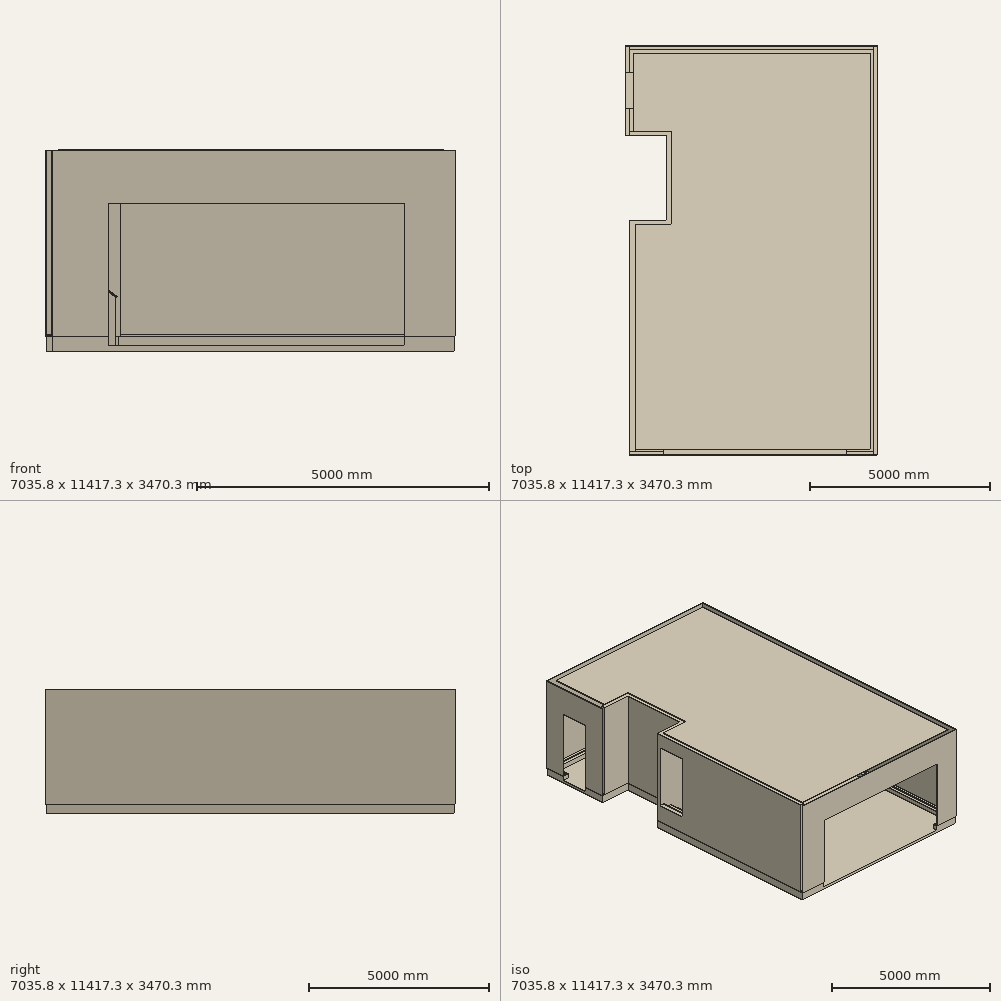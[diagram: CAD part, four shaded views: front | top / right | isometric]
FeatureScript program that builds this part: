
annotation { "Feature Type Name" : "Feature", "Feature Type Description" : "" }
export const myFeature = defineFeature(function(context is Context, id is Id, definition is map)
    precondition{}
    {
        {
            var Q0;
            Q0=qCreatedBy(makeId("Top.planeOp"),FACE);
            var sketch = newSketch(context, id + "F0", { "sketchPlane" : qUnion([Q0])});
            skLineSegment(sketch, "E0.bottom", {"start": v(0, 0) * mm, "end": v(-6597.65, 0) * mm});
            skLineSegment(sketch, "E0.top", {"start": v(0, 11023.6) * mm, "end": v(-6597.65, 11023.6) * mm});
            skLineSegment(sketch, "E0.left", {"start": v(0, 0) * mm, "end": v(0, 11023.6) * mm});
            skLineSegment(sketch, "E0.right", {"start": v(-6597.65, 0) * mm, "end": v(-6597.65, 6286.5) * mm});
            skLineSegment(sketch, "E1", {"start": v(-6597.65, 8839.2) * mm, "end": v(-5568.95, 8839.2) * mm});
            skLineSegment(sketch, "E2", {"start": v(-5568.95, 8839.2) * mm, "end": v(-5568.95, 6286.5) * mm});
            skLineSegment(sketch, "E3", {"start": v(-5568.95, 6286.5) * mm, "end": v(-6597.65, 6286.5) * mm});
            skLineSegment(sketch, "E4", {"start": v(-6597.65, 8839.2) * mm, "end": v(-6597.65, 11023.6) * mm});
            skSolve(sketch);
        }
        {
            var Q0;
            Q0 = qSketchRegion(id + "F0", true);
            extrude(context, id + "F1", {"entities" : qUnion([Q0]), "oppositeDirection" : true, "depth" : 101.6 * mm, "offsetDistance" : 25.4 * mm});
        }
        {
            var Q0;
            Q0=makeQuery(id+"F1.opExtrude","CAP_FACE",FACE,{"disambiguationData":[OSD([sQuery(id+"F0.wireOp",EDGE,"E0.bottom"),sQuery(id+"F0.wireOp",EDGE,"E0.top"),sQuery(id+"F0.wireOp",EDGE,"E0.left"),sQuery(id+"F0.wireOp",EDGE,"E0.right"),sQuery(id+"F0.wireOp",EDGE,"E1"),sQuery(id+"F0.wireOp",EDGE,"E2"),sQuery(id+"F0.wireOp",EDGE,"E3"),sQuery(id+"F0.wireOp",EDGE,"E4")])],"isStart":false});
            var sketch = newSketch(context, id + "F2", { "sketchPlane" : qUnion([Q0])});
            skLineSegment(sketch, "E5.0", {"start": v(190.5, 146.05) * mm, "end": v(-6597.65, 146.05) * mm});
            skLineSegment(sketch, "E6.0", {"start": v(0, -11023.6) * mm, "end": v(-6597.65, -11023.6) * mm});
            skLineSegment(sketch, "E7.0", {"start": v(-6807.2, -8839.2) * mm, "end": v(-6807.2, -11233.15) * mm});
            skLineSegment(sketch, "E7.1", {"start": v(190.5, -11233.15) * mm, "end": v(-6807.2, -11233.15) * mm});
            skLineSegment(sketch, "E8.0", {"start": v(190.5, 146.05) * mm, "end": v(190.5, -11233.15) * mm});
            skLineSegment(sketch, "E9", {"start": v(-6807.2, -8839.2) * mm, "end": v(-6597.65, -8839.2) * mm});
            skLineSegment(sketch, "E10", {"start": v(-6597.65, 146.05) * mm, "end": v(-6597.65, 0) * mm});
            skSolve(sketch);
        }
        {
            var Q0;
            Q0 = qSketchRegion(id + "F2", true);
            var Q1;
            Q1=makeQuery(id+"F2.imprint","IMPRINT",FACE,{"disambiguationData":[TD([[makeQuery(id+"F2.imprint","IMPRINT",EDGE,{"derivedFrom":sQuery(id+"F2.wireOp",EDGE,"E5.0")}),1.0]])]});
            extrude(context, id + "F3", {"entities" : qUnion([Q0, Q1]), "oppositeDirection" : true, "depth" : 254 * mm, "offsetDistance" : 25.4 * mm});
        }
        {
            var Q0;
            Q0=makeQuery(id+"F1.opExtrude","CAP_FACE",FACE,{"disambiguationData":[OSD([sQuery(id+"F0.wireOp",EDGE,"E0.bottom"),sQuery(id+"F0.wireOp",EDGE,"E0.top"),sQuery(id+"F0.wireOp",EDGE,"E0.left"),sQuery(id+"F0.wireOp",EDGE,"E0.right"),sQuery(id+"F0.wireOp",EDGE,"E1"),sQuery(id+"F0.wireOp",EDGE,"E2"),sQuery(id+"F0.wireOp",EDGE,"E3"),sQuery(id+"F0.wireOp",EDGE,"E4")])],"isStart":false});
            var sketch = newSketch(context, id + "F4", { "sketchPlane" : qUnion([Q0])});
            skLineSegment(sketch, "E11.0", {"start": v(-6597.65, -8839.2) * mm, "end": v(-5568.95, -8839.2) * mm});
            skLineSegment(sketch, "E12.0", {"start": v(-5568.95, -8839.2) * mm, "end": v(-5568.95, -6286.5) * mm});
            skLineSegment(sketch, "E13.0", {"start": v(-5568.95, -6286.5) * mm, "end": v(-6597.65, -6286.5) * mm});
            skLineSegment(sketch, "E14.0", {"start": v(-6597.65, 0) * mm, "end": v(-6597.65, -6286.5) * mm});
            skLineSegment(sketch, "E15.0", {"start": v(-6699.25, 146.05) * mm, "end": v(-6699.25, -6388.1) * mm});
            skLineSegment(sketch, "E15.1", {"start": v(-5670.55, -6388.1) * mm, "end": v(-6699.25, -6388.1) * mm});
            skLineSegment(sketch, "E15.2", {"start": v(-5670.55, -8737.6) * mm, "end": v(-5670.55, -6388.1) * mm});
            skLineSegment(sketch, "E15.3", {"start": v(-6807.2, -8737.6) * mm, "end": v(-5670.55, -8737.6) * mm});
            skLineSegment(sketch, "E16.0", {"start": v(-6807.2, -8839.2) * mm, "end": v(-6597.65, -8839.2) * mm});
            skLineSegment(sketch, "E17", {"start": v(-6807.2, -8839.2) * mm, "end": v(-6807.2, -8737.6) * mm});
            skLineSegment(sketch, "E18.0", {"start": v(-6597.65, 146.05) * mm, "end": v(-6597.65, 0) * mm});
            skLineSegment(sketch, "E19", {"start": v(-6597.65, 146.05) * mm, "end": v(-6699.25, 146.05) * mm});
            skSolve(sketch);
        }
        {
            var Q0;
            Q0 = qSketchRegion(id + "F4", true);
            extrude(context, id + "F5", {"entities" : qUnion([Q0]), "oppositeDirection" : true, "depth" : 254 * mm, "offsetDistance" : 25.4 * mm});
        }
        {
            var Q0;
            Q0=makeQuery(id+"F3.opExtrude","CAP_FACE",FACE,{"disambiguationData":[OSD([sQuery(id+"F0.wireOp",EDGE,"E0.bottom"),sQuery(id+"F0.wireOp",EDGE,"E0.left"),sQuery(id+"F0.wireOp",EDGE,"E4"),sQuery(id+"F2.wireOp",EDGE,"E5.0"),sQuery(id+"F2.wireOp",EDGE,"E6.0"),sQuery(id+"F2.wireOp",EDGE,"E7.0"),sQuery(id+"F2.wireOp",EDGE,"E7.1"),sQuery(id+"F2.wireOp",EDGE,"E8.0"),sQuery(id+"F2.wireOp",EDGE,"E9"),sQuery(id+"F2.wireOp",EDGE,"E10")])],"isStart":false});
            var sketch = newSketch(context, id + "F6", { "sketchPlane" : qUnion([Q0])});
            skLineSegment(sketch, "E20.bottom", {"start": v(-5746.75, 0) * mm, "end": v(-660.4, 0) * mm});
            skLineSegment(sketch, "E20.top", {"start": v(-5746.75, -146.05) * mm, "end": v(-660.4, -146.05) * mm});
            skLineSegment(sketch, "E20.left", {"start": v(-5746.75, 0) * mm, "end": v(-5746.75, -146.05) * mm});
            skLineSegment(sketch, "E20.right", {"start": v(-660.4, 0) * mm, "end": v(-660.4, -146.05) * mm});
            skSolve(sketch);
        }
        {
            var Q0;
            Q0 = qSketchRegion(id + "F6", true);
            extrude(context, id + "F7", {"entities" : qUnion([Q0]), "operationType" : NewBodyOperationType.REMOVE, "depth" : -152.4 * mm, "offsetDistance" : 25.4 * mm});
        }
        {
            var Q0;
            Q0=makeQuery(id+"F1.opExtrude","SWEPT_BODY",BODY,{"disambiguationData":[OSD([sQuery(id+"F0.wireOp",EDGE,"E0.bottom"),sQuery(id+"F0.wireOp",EDGE,"E0.top"),sQuery(id+"F0.wireOp",EDGE,"E0.left"),sQuery(id+"F0.wireOp",EDGE,"E0.right"),sQuery(id+"F0.wireOp",EDGE,"E1"),sQuery(id+"F0.wireOp",EDGE,"E2"),sQuery(id+"F0.wireOp",EDGE,"E3"),sQuery(id+"F0.wireOp",EDGE,"E4")])]});
            var Q1;
            Q1=makeQuery(id+"F3.opExtrude","SWEPT_BODY",BODY,{"disambiguationData":[OSD([sQuery(id+"F0.wireOp",EDGE,"E0.bottom"),sQuery(id+"F0.wireOp",EDGE,"E0.left"),sQuery(id+"F0.wireOp",EDGE,"E4"),sQuery(id+"F2.wireOp",EDGE,"E5.0"),sQuery(id+"F2.wireOp",EDGE,"E6.0"),sQuery(id+"F2.wireOp",EDGE,"E7.0"),sQuery(id+"F2.wireOp",EDGE,"E7.1"),sQuery(id+"F2.wireOp",EDGE,"E8.0"),sQuery(id+"F2.wireOp",EDGE,"E9"),sQuery(id+"F2.wireOp",EDGE,"E10")])]});
            var Q2;
            Q2=makeQuery(id+"F5.opExtrude","SWEPT_BODY",BODY,{"disambiguationData":[OSD([sQuery(id+"F4.wireOp",EDGE,"E11.0"),sQuery(id+"F4.wireOp",EDGE,"E12.0"),sQuery(id+"F4.wireOp",EDGE,"E13.0"),sQuery(id+"F4.wireOp",EDGE,"E14.0"),sQuery(id+"F4.wireOp",EDGE,"E15.0"),sQuery(id+"F4.wireOp",EDGE,"E15.1"),sQuery(id+"F4.wireOp",EDGE,"E15.2"),sQuery(id+"F4.wireOp",EDGE,"E15.3"),sQuery(id+"F4.wireOp",EDGE,"E16.0"),sQuery(id+"F4.wireOp",EDGE,"E17"),sQuery(id+"F4.wireOp",EDGE,"E18.0"),sQuery(id+"F4.wireOp",EDGE,"E19")])]});
            booleanBodies(context, id + "F8", {"operationType" : BooleanOperationType.UNION, "tools" : qUnion([Q0, Q1, Q2])});
        }
        {
            var Q0;
            {var subQ0=sQuery(id+"F2.wireOp",EDGE,"E5.0");var subQ2=sQuery(id+"F2.wireOp",EDGE,"E10");var subQ3=sQuery(id+"F0.wireOp",EDGE,"E0.bottom");var subQ5=sQuery(id+"F2.wireOp",EDGE,"E9");var subQ6=sQuery(id+"F2.wireOp",EDGE,"E8.0");var subQ7=sQuery(id+"F2.wireOp",EDGE,"E7.1");var subQ8=sQuery(id+"F2.wireOp",EDGE,"E7.0");var subQ9=sQuery(id+"F2.wireOp",EDGE,"E6.0");var subQ10=sQuery(id+"F0.wireOp",EDGE,"E4");var subQ11=sQuery(id+"F0.wireOp",EDGE,"E0.left");var subQ12=makeQuery(id+"F3.opExtrude","CAP_FACE",FACE,{"disambiguationData":[OSD([subQ3,subQ11,subQ10,subQ0,subQ9,subQ8,subQ7,subQ6,subQ5,subQ2])],"isStart":false});Q0=makeQuery(id+"F8.opBoolean","MERGE",FACE,{"derivedFrom":[makeQuery(id+"F5.opExtrude","CAP_FACE",FACE,{"disambiguationData":[OSD([sQuery(id+"F4.wireOp",EDGE,"E11.0"),sQuery(id+"F4.wireOp",EDGE,"E12.0"),sQuery(id+"F4.wireOp",EDGE,"E13.0"),sQuery(id+"F4.wireOp",EDGE,"E14.0"),sQuery(id+"F4.wireOp",EDGE,"E15.0"),sQuery(id+"F4.wireOp",EDGE,"E15.1"),sQuery(id+"F4.wireOp",EDGE,"E15.2"),sQuery(id+"F4.wireOp",EDGE,"E15.3"),sQuery(id+"F4.wireOp",EDGE,"E16.0"),sQuery(id+"F4.wireOp",EDGE,"E17"),sQuery(id+"F4.wireOp",EDGE,"E18.0"),sQuery(id+"F4.wireOp",EDGE,"E19")])],"isStart":false}),makeQuery(id+"F7.boolean.opBoolean","SPLIT",FACE,{"disambiguationData":[TD([makeQuery(id+"F3.opExtrude","SWEPT_FACE",FACE,{"disambiguationData":[OSD([subQ9])]})])],"derivedFrom":subQ12}),makeQuery(id+"F7.boolean.opBoolean","SPLIT",FACE,{"disambiguationData":[TD([makeQuery(id+"F3.opExtrude","SWEPT_FACE",FACE,{"disambiguationData":[OSD([subQ2])]})])],"derivedFrom":subQ12})]});}
            var sketch = newSketch(context, id + "F9", { "sketchPlane" : qUnion([Q0])});
            skLineSegment(sketch, "E21.bottom", {"start": v(-6807.2, 10490.2) * mm, "end": v(-6597.65, 10490.2) * mm});
            skLineSegment(sketch, "E21.top", {"start": v(-6807.2, 9499.6) * mm, "end": v(-6597.65, 9499.6) * mm});
            skLineSegment(sketch, "E21.left", {"start": v(-6807.2, 10490.2) * mm, "end": v(-6807.2, 9499.6) * mm});
            skLineSegment(sketch, "E21.right", {"start": v(-6597.65, 10490.2) * mm, "end": v(-6597.65, 9499.6) * mm});
            skSolve(sketch);
        }
        {
            var Q0;
            Q0=makeQuery(id+"F9.imprint","IMPRINT",FACE,{"disambiguationData":[TD([[makeQuery(id+"F9.imprint","IMPRINT",EDGE,{"derivedFrom":sQuery(id+"F9.wireOp",EDGE,"E21.bottom")}),-1.0]])]});
            extrude(context, id + "F10", {"entities" : qUnion([Q0]), "operationType" : NewBodyOperationType.REMOVE, "oppositeDirection" : true, "depth" : 152.4 * mm, "offsetDistance" : 25.4 * mm});
        }
        {
            var Q0;
            {var subQ0=sQuery(id+"F4.wireOp",EDGE,"E19");var subQ1=sQuery(id+"F0.wireOp",EDGE,"E0.left");var subQ3=sQuery(id+"F0.wireOp",EDGE,"E0.bottom");var subQ5=sQuery(id+"F2.wireOp",EDGE,"E8.0");var subQ7=sQuery(id+"F4.wireOp",EDGE,"E17");var subQ8=sQuery(id+"F0.wireOp",EDGE,"E4");var subQ10=sQuery(id+"F2.wireOp",EDGE,"E5.0");var subQ12=sQuery(id+"F2.wireOp",EDGE,"E7.1");var subQ14=sQuery(id+"F2.wireOp",EDGE,"E6.0");var subQ15=makeQuery(id+"F3.opExtrude","SWEPT_FACE",FACE,{"disambiguationData":[OSD([subQ14])]});var subQ16=sQuery(id+"F2.wireOp",EDGE,"E7.0");var subQ19=sQuery(id+"F2.wireOp",EDGE,"E10");var subQ20=sQuery(id+"F2.wireOp",EDGE,"E9");var subQ21=makeQuery(id+"F3.opExtrude","CAP_FACE",FACE,{"disambiguationData":[OSD([subQ3,subQ1,subQ8,subQ10,subQ14,subQ16,subQ12,subQ5,subQ20,subQ19])],"isStart":false});Q0=makeQuery(id+"F10.boolean.opBoolean","SPLIT",FACE,{"disambiguationData":[TD([subQ15])],"derivedFrom":makeQuery(id+"F8.opBoolean","MERGE",FACE,{"derivedFrom":[makeQuery(id+"F5.opExtrude","CAP_FACE",FACE,{"disambiguationData":[OSD([sQuery(id+"F4.wireOp",EDGE,"E11.0"),sQuery(id+"F4.wireOp",EDGE,"E12.0"),sQuery(id+"F4.wireOp",EDGE,"E13.0"),sQuery(id+"F4.wireOp",EDGE,"E14.0"),sQuery(id+"F4.wireOp",EDGE,"E15.0"),sQuery(id+"F4.wireOp",EDGE,"E15.1"),sQuery(id+"F4.wireOp",EDGE,"E15.2"),sQuery(id+"F4.wireOp",EDGE,"E15.3"),sQuery(id+"F4.wireOp",EDGE,"E16.0"),subQ7,sQuery(id+"F4.wireOp",EDGE,"E18.0"),subQ0])],"isStart":false}),makeQuery(id+"F7.boolean.opBoolean","SPLIT",FACE,{"disambiguationData":[TD([subQ15])],"derivedFrom":subQ21}),makeQuery(id+"F7.boolean.opBoolean","SPLIT",FACE,{"disambiguationData":[TD([makeQuery(id+"F3.opExtrude","SWEPT_FACE",FACE,{"disambiguationData":[OSD([subQ19])]})])],"derivedFrom":subQ21})]})});}
            var sketch = newSketch(context, id + "F11", { "sketchPlane" : qUnion([Q0])});
            skLineSegment(sketch, "E22.bottom", {"start": v(190.5, 11233.15) * mm, "end": v(101.6, 11233.15) * mm});
            skLineSegment(sketch, "E22.top", {"start": v(190.5, -146.05) * mm, "end": v(101.6, -146.05) * mm});
            skLineSegment(sketch, "E22.left", {"start": v(190.5, 11233.15) * mm, "end": v(190.5, -146.05) * mm});
            skLineSegment(sketch, "E22.right", {"start": v(101.6, 11233.15) * mm, "end": v(101.6, -146.05) * mm});
            skSolve(sketch);
        }
        {
            var Q0;
            Q0 = qSketchRegion(id + "F11", true);
            extrude(context, id + "F12", {"entities" : qUnion([Q0]), "depth" : 38.1 * mm, "offsetDistance" : 25.4 * mm});
        }
        {
            var Q0;
            {var subQ0=sQuery(id+"F4.wireOp",EDGE,"E19");var subQ1=sQuery(id+"F0.wireOp",EDGE,"E0.left");var subQ3=sQuery(id+"F0.wireOp",EDGE,"E0.bottom");var subQ5=sQuery(id+"F2.wireOp",EDGE,"E8.0");var subQ7=sQuery(id+"F4.wireOp",EDGE,"E17");var subQ8=sQuery(id+"F0.wireOp",EDGE,"E4");var subQ10=sQuery(id+"F2.wireOp",EDGE,"E5.0");var subQ12=sQuery(id+"F2.wireOp",EDGE,"E7.1");var subQ14=sQuery(id+"F2.wireOp",EDGE,"E6.0");var subQ15=makeQuery(id+"F3.opExtrude","SWEPT_FACE",FACE,{"disambiguationData":[OSD([subQ14])]});var subQ16=sQuery(id+"F2.wireOp",EDGE,"E7.0");var subQ19=sQuery(id+"F2.wireOp",EDGE,"E10");var subQ20=sQuery(id+"F2.wireOp",EDGE,"E9");var subQ21=makeQuery(id+"F3.opExtrude","CAP_FACE",FACE,{"disambiguationData":[OSD([subQ3,subQ1,subQ8,subQ10,subQ14,subQ16,subQ12,subQ5,subQ20,subQ19])],"isStart":false});Q0=makeQuery(id+"F10.boolean.opBoolean","SPLIT",FACE,{"disambiguationData":[TD([subQ15])],"derivedFrom":makeQuery(id+"F8.opBoolean","MERGE",FACE,{"derivedFrom":[makeQuery(id+"F5.opExtrude","CAP_FACE",FACE,{"disambiguationData":[OSD([sQuery(id+"F4.wireOp",EDGE,"E11.0"),sQuery(id+"F4.wireOp",EDGE,"E12.0"),sQuery(id+"F4.wireOp",EDGE,"E13.0"),sQuery(id+"F4.wireOp",EDGE,"E14.0"),sQuery(id+"F4.wireOp",EDGE,"E15.0"),sQuery(id+"F4.wireOp",EDGE,"E15.1"),sQuery(id+"F4.wireOp",EDGE,"E15.2"),sQuery(id+"F4.wireOp",EDGE,"E15.3"),sQuery(id+"F4.wireOp",EDGE,"E16.0"),subQ7,sQuery(id+"F4.wireOp",EDGE,"E18.0"),subQ0])],"isStart":false}),makeQuery(id+"F7.boolean.opBoolean","SPLIT",FACE,{"disambiguationData":[TD([subQ15])],"derivedFrom":subQ21}),makeQuery(id+"F7.boolean.opBoolean","SPLIT",FACE,{"disambiguationData":[TD([makeQuery(id+"F3.opExtrude","SWEPT_FACE",FACE,{"disambiguationData":[OSD([subQ19])]})])],"derivedFrom":subQ21})]})});}
            var sketch = newSketch(context, id + "F13", { "sketchPlane" : qUnion([Q0])});
            skLineSegment(sketch, "E23.bottom", {"start": v(-6807.2, 10490.2) * mm, "end": v(-6718.3, 10490.2) * mm});
            skLineSegment(sketch, "E23.top", {"start": v(-6807.2, 11233.15) * mm, "end": v(-6718.3, 11233.15) * mm});
            skLineSegment(sketch, "E23.left", {"start": v(-6807.2, 10490.2) * mm, "end": v(-6807.2, 11233.15) * mm});
            skLineSegment(sketch, "E23.right", {"start": v(-6718.3, 10490.2) * mm, "end": v(-6718.3, 11233.15) * mm});
            skSolve(sketch);
        }
        {
            var Q0;
            Q0 = qSketchRegion(id + "F13", true);
            extrude(context, id + "F14", {"entities" : qUnion([Q0]), "depth" : 38.1 * mm, "offsetDistance" : 25.4 * mm});
        }
        {
            var Q0;
            {var subQ0=sQuery(id+"F4.wireOp",EDGE,"E15.1");var subQ1=sQuery(id+"F0.wireOp",EDGE,"E4");var subQ3=sQuery(id+"F4.wireOp",EDGE,"E15.0");var subQ4=sQuery(id+"F4.wireOp",EDGE,"E18.0");var subQ5=sQuery(id+"F4.wireOp",EDGE,"E14.0");var subQ6=sQuery(id+"F0.wireOp",EDGE,"E0.bottom");var subQ8=sQuery(id+"F4.wireOp",EDGE,"E13.0");var subQ9=sQuery(id+"F4.wireOp",EDGE,"E16.0");var subQ10=sQuery(id+"F4.wireOp",EDGE,"E11.0");var subQ11=sQuery(id+"F4.wireOp",EDGE,"E12.0");var subQ12=sQuery(id+"F2.wireOp",EDGE,"E7.0");var subQ14=sQuery(id+"F2.wireOp",EDGE,"E5.0");var subQ16=sQuery(id+"F4.wireOp",EDGE,"E15.2");var subQ17=sQuery(id+"F4.wireOp",EDGE,"E15.3");var subQ18=sQuery(id+"F4.wireOp",EDGE,"E17");var subQ19=sQuery(id+"F4.wireOp",EDGE,"E19");var subQ21=sQuery(id+"F2.wireOp",EDGE,"E10");var subQ22=sQuery(id+"F2.wireOp",EDGE,"E9");var subQ23=sQuery(id+"F2.wireOp",EDGE,"E8.0");var subQ24=sQuery(id+"F2.wireOp",EDGE,"E7.1");var subQ25=sQuery(id+"F2.wireOp",EDGE,"E6.0");var subQ26=sQuery(id+"F0.wireOp",EDGE,"E0.left");var subQ27=makeQuery(id+"F3.opExtrude","CAP_FACE",FACE,{"disambiguationData":[OSD([subQ6,subQ26,subQ1,subQ14,subQ25,subQ12,subQ24,subQ23,subQ22,subQ21])],"isStart":false});Q0=makeQuery(id+"F10.boolean.opBoolean","SPLIT",FACE,{"disambiguationData":[TD([makeQuery(id+"F5.opExtrude","SWEPT_FACE",FACE,{"disambiguationData":[OSD([subQ11])]})])],"derivedFrom":makeQuery(id+"F8.opBoolean","MERGE",FACE,{"derivedFrom":[makeQuery(id+"F5.opExtrude","CAP_FACE",FACE,{"disambiguationData":[OSD([subQ10,subQ11,subQ8,subQ5,subQ3,subQ0,subQ16,subQ17,subQ9,subQ18,subQ4,subQ19])],"isStart":false}),makeQuery(id+"F7.boolean.opBoolean","SPLIT",FACE,{"disambiguationData":[TD([makeQuery(id+"F3.opExtrude","SWEPT_FACE",FACE,{"disambiguationData":[OSD([subQ25])]})])],"derivedFrom":subQ27}),makeQuery(id+"F7.boolean.opBoolean","SPLIT",FACE,{"disambiguationData":[TD([makeQuery(id+"F3.opExtrude","SWEPT_FACE",FACE,{"disambiguationData":[OSD([subQ21])]})])],"derivedFrom":subQ27})]})});}
            var sketch = newSketch(context, id + "F15", { "sketchPlane" : qUnion([Q0])});
            skLineSegment(sketch, "E24.bottom", {"start": v(-6807.2, 9499.6) * mm, "end": v(-6718.3, 9499.6) * mm});
            skLineSegment(sketch, "E24.top", {"start": v(-6807.2, 8737.6) * mm, "end": v(-6718.3, 8737.6) * mm});
            skLineSegment(sketch, "E24.left", {"start": v(-6807.2, 9499.6) * mm, "end": v(-6807.2, 8737.6) * mm});
            skLineSegment(sketch, "E24.right", {"start": v(-6718.3, 9499.6) * mm, "end": v(-6718.3, 8737.6) * mm});
            skSolve(sketch);
        }
        {
            var Q0;
            Q0 = qSketchRegion(id + "F15", true);
            extrude(context, id + "F16", {"entities" : qUnion([Q0]), "depth" : 25.4 * mm, "offsetDistance" : 25.4 * mm});
        }
        {
            var Q0;
            {var subQ0=sQuery(id+"F4.wireOp",EDGE,"E19");var subQ1=sQuery(id+"F0.wireOp",EDGE,"E0.left");var subQ3=sQuery(id+"F0.wireOp",EDGE,"E0.bottom");var subQ5=sQuery(id+"F2.wireOp",EDGE,"E8.0");var subQ7=sQuery(id+"F4.wireOp",EDGE,"E17");var subQ8=sQuery(id+"F0.wireOp",EDGE,"E4");var subQ10=sQuery(id+"F2.wireOp",EDGE,"E5.0");var subQ12=sQuery(id+"F2.wireOp",EDGE,"E7.1");var subQ14=sQuery(id+"F2.wireOp",EDGE,"E6.0");var subQ15=makeQuery(id+"F3.opExtrude","SWEPT_FACE",FACE,{"disambiguationData":[OSD([subQ14])]});var subQ16=sQuery(id+"F2.wireOp",EDGE,"E7.0");var subQ19=sQuery(id+"F2.wireOp",EDGE,"E10");var subQ20=sQuery(id+"F2.wireOp",EDGE,"E9");var subQ21=makeQuery(id+"F3.opExtrude","CAP_FACE",FACE,{"disambiguationData":[OSD([subQ3,subQ1,subQ8,subQ10,subQ14,subQ16,subQ12,subQ5,subQ20,subQ19])],"isStart":false});Q0=makeQuery(id+"F10.boolean.opBoolean","SPLIT",FACE,{"disambiguationData":[TD([subQ15])],"derivedFrom":makeQuery(id+"F8.opBoolean","MERGE",FACE,{"derivedFrom":[makeQuery(id+"F5.opExtrude","CAP_FACE",FACE,{"disambiguationData":[OSD([sQuery(id+"F4.wireOp",EDGE,"E11.0"),sQuery(id+"F4.wireOp",EDGE,"E12.0"),sQuery(id+"F4.wireOp",EDGE,"E13.0"),sQuery(id+"F4.wireOp",EDGE,"E14.0"),sQuery(id+"F4.wireOp",EDGE,"E15.0"),sQuery(id+"F4.wireOp",EDGE,"E15.1"),sQuery(id+"F4.wireOp",EDGE,"E15.2"),sQuery(id+"F4.wireOp",EDGE,"E15.3"),sQuery(id+"F4.wireOp",EDGE,"E16.0"),subQ7,sQuery(id+"F4.wireOp",EDGE,"E18.0"),subQ0])],"isStart":false}),makeQuery(id+"F7.boolean.opBoolean","SPLIT",FACE,{"disambiguationData":[TD([subQ15])],"derivedFrom":subQ21}),makeQuery(id+"F7.boolean.opBoolean","SPLIT",FACE,{"disambiguationData":[TD([makeQuery(id+"F3.opExtrude","SWEPT_FACE",FACE,{"disambiguationData":[OSD([subQ19])]})])],"derivedFrom":subQ21})]})});}
            var sketch = newSketch(context, id + "F17", { "sketchPlane" : qUnion([Q0])});
            skLineSegment(sketch, "E25.0", {"start": v(-6718.3, 10490.2) * mm, "end": v(-6718.3, 11233.15) * mm});
            skLineSegment(sketch, "E26.bottom", {"start": v(-6718.3, 11233.15) * mm, "end": v(101.6, 11233.15) * mm});
            skLineSegment(sketch, "E26.top", {"start": v(-6718.3, 11144.25) * mm, "end": v(101.6, 11144.25) * mm});
            skLineSegment(sketch, "E26.left", {"start": v(-6718.3, 11233.15) * mm, "end": v(-6718.3, 11144.25) * mm});
            skLineSegment(sketch, "E26.right", {"start": v(101.6, 11233.15) * mm, "end": v(101.6, 11144.25) * mm});
            skPoint(sketch, "E27.0", {"position": v(101.6, 11233.15) * mm});
            skSolve(sketch);
        }
        {
            var Q0;
            Q0 = qSketchRegion(id + "F17", true);
            extrude(context, id + "F18", {"entities" : qUnion([Q0]), "depth" : 38.1 * mm, "offsetDistance" : 25.4 * mm});
        }
        {
            var Q0;
            {var subQ0=sQuery(id+"F4.wireOp",EDGE,"E19");var subQ1=sQuery(id+"F0.wireOp",EDGE,"E0.left");var subQ3=sQuery(id+"F0.wireOp",EDGE,"E0.bottom");var subQ5=sQuery(id+"F2.wireOp",EDGE,"E8.0");var subQ7=sQuery(id+"F4.wireOp",EDGE,"E17");var subQ8=sQuery(id+"F0.wireOp",EDGE,"E4");var subQ10=sQuery(id+"F2.wireOp",EDGE,"E5.0");var subQ12=sQuery(id+"F2.wireOp",EDGE,"E7.1");var subQ14=sQuery(id+"F2.wireOp",EDGE,"E6.0");var subQ15=makeQuery(id+"F3.opExtrude","SWEPT_FACE",FACE,{"disambiguationData":[OSD([subQ14])]});var subQ16=sQuery(id+"F2.wireOp",EDGE,"E7.0");var subQ19=sQuery(id+"F2.wireOp",EDGE,"E10");var subQ20=sQuery(id+"F2.wireOp",EDGE,"E9");var subQ21=makeQuery(id+"F3.opExtrude","CAP_FACE",FACE,{"disambiguationData":[OSD([subQ3,subQ1,subQ8,subQ10,subQ14,subQ16,subQ12,subQ5,subQ20,subQ19])],"isStart":false});Q0=makeQuery(id+"F10.boolean.opBoolean","SPLIT",FACE,{"disambiguationData":[TD([subQ15])],"derivedFrom":makeQuery(id+"F8.opBoolean","MERGE",FACE,{"derivedFrom":[makeQuery(id+"F5.opExtrude","CAP_FACE",FACE,{"disambiguationData":[OSD([sQuery(id+"F4.wireOp",EDGE,"E11.0"),sQuery(id+"F4.wireOp",EDGE,"E12.0"),sQuery(id+"F4.wireOp",EDGE,"E13.0"),sQuery(id+"F4.wireOp",EDGE,"E14.0"),sQuery(id+"F4.wireOp",EDGE,"E15.0"),sQuery(id+"F4.wireOp",EDGE,"E15.1"),sQuery(id+"F4.wireOp",EDGE,"E15.2"),sQuery(id+"F4.wireOp",EDGE,"E15.3"),sQuery(id+"F4.wireOp",EDGE,"E16.0"),subQ7,sQuery(id+"F4.wireOp",EDGE,"E18.0"),subQ0])],"isStart":false}),makeQuery(id+"F7.boolean.opBoolean","SPLIT",FACE,{"disambiguationData":[TD([subQ15])],"derivedFrom":subQ21}),makeQuery(id+"F7.boolean.opBoolean","SPLIT",FACE,{"disambiguationData":[TD([makeQuery(id+"F3.opExtrude","SWEPT_FACE",FACE,{"disambiguationData":[OSD([subQ19])]})])],"derivedFrom":subQ21})]})});}
            var sketch = newSketch(context, id + "F19", { "sketchPlane" : qUnion([Q0])});
            skPoint(sketch, "E28.0", {"position": v(101.6, -146.05) * mm});
            skPoint(sketch, "E29.0", {"position": v(-660.4, -146.05) * mm});
            skLineSegment(sketch, "E30.bottom", {"start": v(-660.4, -146.05) * mm, "end": v(101.6, -146.05) * mm});
            skLineSegment(sketch, "E30.top", {"start": v(-660.4, -57.15) * mm, "end": v(101.6, -57.15) * mm});
            skLineSegment(sketch, "E30.left", {"start": v(-660.4, -146.05) * mm, "end": v(-660.4, -57.15) * mm});
            skLineSegment(sketch, "E30.right", {"start": v(101.6, -146.05) * mm, "end": v(101.6, -57.15) * mm});
            skSolve(sketch);
        }
        {
            var Q0;
            Q0 = qSketchRegion(id + "F19", true);
            extrude(context, id + "F20", {"entities" : qUnion([Q0]), "depth" : 38.1 * mm, "offsetDistance" : 25.4 * mm});
        }
        {
            var Q0;
            {var subQ0=sQuery(id+"F4.wireOp",EDGE,"E15.1");var subQ1=sQuery(id+"F0.wireOp",EDGE,"E4");var subQ3=sQuery(id+"F4.wireOp",EDGE,"E15.0");var subQ4=sQuery(id+"F4.wireOp",EDGE,"E18.0");var subQ5=sQuery(id+"F4.wireOp",EDGE,"E14.0");var subQ6=sQuery(id+"F0.wireOp",EDGE,"E0.bottom");var subQ8=sQuery(id+"F4.wireOp",EDGE,"E13.0");var subQ9=sQuery(id+"F4.wireOp",EDGE,"E16.0");var subQ10=sQuery(id+"F4.wireOp",EDGE,"E11.0");var subQ11=sQuery(id+"F4.wireOp",EDGE,"E12.0");var subQ12=sQuery(id+"F2.wireOp",EDGE,"E7.0");var subQ14=sQuery(id+"F2.wireOp",EDGE,"E5.0");var subQ16=sQuery(id+"F4.wireOp",EDGE,"E15.2");var subQ17=sQuery(id+"F4.wireOp",EDGE,"E15.3");var subQ18=sQuery(id+"F4.wireOp",EDGE,"E17");var subQ19=sQuery(id+"F4.wireOp",EDGE,"E19");var subQ21=sQuery(id+"F2.wireOp",EDGE,"E10");var subQ22=sQuery(id+"F2.wireOp",EDGE,"E9");var subQ23=sQuery(id+"F2.wireOp",EDGE,"E8.0");var subQ24=sQuery(id+"F2.wireOp",EDGE,"E7.1");var subQ25=sQuery(id+"F2.wireOp",EDGE,"E6.0");var subQ26=sQuery(id+"F0.wireOp",EDGE,"E0.left");var subQ27=makeQuery(id+"F3.opExtrude","CAP_FACE",FACE,{"disambiguationData":[OSD([subQ6,subQ26,subQ1,subQ14,subQ25,subQ12,subQ24,subQ23,subQ22,subQ21])],"isStart":false});Q0=makeQuery(id+"F10.boolean.opBoolean","SPLIT",FACE,{"disambiguationData":[TD([makeQuery(id+"F5.opExtrude","SWEPT_FACE",FACE,{"disambiguationData":[OSD([subQ11])]})])],"derivedFrom":makeQuery(id+"F8.opBoolean","MERGE",FACE,{"derivedFrom":[makeQuery(id+"F5.opExtrude","CAP_FACE",FACE,{"disambiguationData":[OSD([subQ10,subQ11,subQ8,subQ5,subQ3,subQ0,subQ16,subQ17,subQ9,subQ18,subQ4,subQ19])],"isStart":false}),makeQuery(id+"F7.boolean.opBoolean","SPLIT",FACE,{"disambiguationData":[TD([makeQuery(id+"F3.opExtrude","SWEPT_FACE",FACE,{"disambiguationData":[OSD([subQ25])]})])],"derivedFrom":subQ27}),makeQuery(id+"F7.boolean.opBoolean","SPLIT",FACE,{"disambiguationData":[TD([makeQuery(id+"F3.opExtrude","SWEPT_FACE",FACE,{"disambiguationData":[OSD([subQ21])]})])],"derivedFrom":subQ27})]})});}
            var sketch = newSketch(context, id + "F21", { "sketchPlane" : qUnion([Q0])});
            skLineSegment(sketch, "E31.bottom", {"start": v(-6699.25, -146.05) * mm, "end": v(-5746.75, -146.05) * mm});
            skLineSegment(sketch, "E31.top", {"start": v(-6699.25, -57.15) * mm, "end": v(-5746.75, -57.15) * mm});
            skLineSegment(sketch, "E31.left", {"start": v(-6699.25, -146.05) * mm, "end": v(-6699.25, -57.15) * mm});
            skLineSegment(sketch, "E31.right", {"start": v(-5746.75, -146.05) * mm, "end": v(-5746.75, -57.15) * mm});
            skSolve(sketch);
        }
        {
            var Q0;
            Q0 = qSketchRegion(id + "F21", true);
            extrude(context, id + "F22", {"entities" : qUnion([Q0]), "depth" : 38.1 * mm, "offsetDistance" : 25.4 * mm});
        }
        {
            var Q0;
            Q0=makeQuery(id+"F5.opExtrude","SWEPT_FACE",FACE,{"disambiguationData":[OSD([sQuery(id+"F4.wireOp",EDGE,"E13.0")])]});
            cPlane(context, id + "F23", {"entities" : qUnion([Q0]), "cplaneType" : CPlaneType.OFFSET, "offset" : 31.75 * mm, "width" : 152.4 * mm, "height" : 152.4 * mm});
        }
        {
            var Q0;
            Q0=qCreatedBy(id+"F23.planeOp",FACE);
            var sketch = newSketch(context, id + "F24", { "sketchPlane" : qUnion([Q0])});
            skLineSegment(sketch, "E32", {"start": v(-5746.75, 0) * mm, "end": v(-5746.75, 165.1) * mm});
            skLineSegment(sketch, "E33", {"start": v(-5746.75, 165.1) * mm, "end": v(-5708.65, 165.1) * mm});
            skLineSegment(sketch, "E34", {"start": v(-5708.65, 165.1) * mm, "end": v(-5708.65, 203.2) * mm});
            skLineSegment(sketch, "E35", {"start": v(-5708.65, 203.2) * mm, "end": v(-5994.4, 203.2) * mm});
            skLineSegment(sketch, "E36", {"start": v(-5994.4, 203.2) * mm, "end": v(-5994.4, 361.95) * mm});
            skLineSegment(sketch, "E37", {"start": v(-5994.4, 361.95) * mm, "end": v(-5962.65, 361.95) * mm});
            skLineSegment(sketch, "E38", {"start": v(-5962.65, 361.95) * mm, "end": v(-5962.65, 400.05) * mm});
            skLineSegment(sketch, "E39", {"start": v(-5962.65, 400.05) * mm, "end": v(-6248.4, 400.05) * mm});
            skLineSegment(sketch, "E40", {"start": v(-6248.4, 400.05) * mm, "end": v(-6248.4, 565.15) * mm});
            skLineSegment(sketch, "E41", {"start": v(-6248.4, 565.15) * mm, "end": v(-6235.7, 565.15) * mm});
            skLineSegment(sketch, "E42", {"start": v(-6235.7, 565.15) * mm, "end": v(-6235.7, 603.25) * mm});
            skLineSegment(sketch, "E43", {"start": v(-6235.7, 603.25) * mm, "end": v(-6521.45, 603.25) * mm});
            skLineSegment(sketch, "E44", {"start": v(-6546.85, 0) * mm, "end": v(-5746.75, 0) * mm});
            skLineSegment(sketch, "E45", {"start": v(-6521.45, 603.25) * mm, "end": v(-6521.45, 755.65) * mm});
            skLineSegment(sketch, "E46", {"start": v(-6521.45, 755.65) * mm, "end": v(-6546.85, 755.65) * mm});
            skLineSegment(sketch, "E47", {"start": v(-6546.85, 755.65) * mm, "end": v(-6546.85, 0) * mm});
            skLineSegment(sketch, "E48.0", {"start": v(-6597.65, 152.4) * mm, "end": v(-6597.65, 0) * mm});
            skSolve(sketch);
        }
        {
            var Q0;
            {var subQ0=sQuery(id+"F24.wireOp",EDGE,"E44");Q0=makeQuery(id+"F24.imprint","IMPRINT",FACE,{"disambiguationData":[TD([[makeQuery(id+"F24.imprint","IMPRINT",EDGE,{"derivedFrom":subQ0}),-1.0]])]});}
            var Q1;
            {var subQ0=sQuery(id+"F24.wireOp",EDGE,"E33");Q1=makeQuery(id+"F24.imprint","IMPRINT",FACE,{"disambiguationData":[TD([[makeQuery(id+"F24.imprint","IMPRINT",EDGE,{"derivedFrom":subQ0}),1.0]])]});}
            extrude(context, id + "F25", {"entities" : qUnion([Q0, Q1]), "depth" : 1003.3 * mm, "offsetDistance" : 25.4 * mm});
        }
        {
            var Q0;
            Q0=makeQuery(id+"F25.opExtrude","CAP_FACE",FACE,{"disambiguationData":[OSD([sQuery(id+"F24.wireOp",EDGE,"E32"),sQuery(id+"F24.wireOp",EDGE,"E33"),sQuery(id+"F24.wireOp",EDGE,"E34"),sQuery(id+"F24.wireOp",EDGE,"E35"),sQuery(id+"F24.wireOp",EDGE,"E36"),sQuery(id+"F24.wireOp",EDGE,"E37"),sQuery(id+"F24.wireOp",EDGE,"E38"),sQuery(id+"F24.wireOp",EDGE,"E39"),sQuery(id+"F24.wireOp",EDGE,"E40"),sQuery(id+"F24.wireOp",EDGE,"E41"),sQuery(id+"F24.wireOp",EDGE,"E42"),sQuery(id+"F24.wireOp",EDGE,"E43"),sQuery(id+"F24.wireOp",EDGE,"E44"),sQuery(id+"F24.wireOp",EDGE,"E45"),sQuery(id+"F24.wireOp",EDGE,"E46"),sQuery(id+"F24.wireOp",EDGE,"E47"),sQuery(id+"F24.wireOp",EDGE,"E48.0")])],"isStart":false});
            var sketch = newSketch(context, id + "F26", { "sketchPlane" : qUnion([Q0])});
            skLineSegment(sketch, "E49", {"start": v(-6546.85, 0) * mm, "end": v(-5632.45, 0) * mm});
            skLineSegment(sketch, "E50", {"start": v(-5632.45, 0) * mm, "end": v(-5632.45, 844.55) * mm});
            skLineSegment(sketch, "E51", {"start": v(-5632.45, 844.55) * mm, "end": v(-6546.85, 1479.55) * mm});
            skLineSegment(sketch, "E52", {"start": v(-6546.85, 1479.55) * mm, "end": v(-6546.85, 0) * mm});
            skSolve(sketch);
        }
        {
            var Q0;
            {var subQ2=sQuery(id+"F26.wireOp",EDGE,"E50");Q0=makeQuery(id+"F26.imprint","IMPRINT",FACE,{"disambiguationData":[TD([[makeQuery(id+"F26.imprint","IMPRINT",EDGE,{"derivedFrom":subQ2}),1.0]])]});}
            var Q1;
            {var subQ3=makeQuery(id+"F25.opExtrude","CAP_EDGE",EDGE,{"disambiguationData":[OSD([sQuery(id+"F24.wireOp",EDGE,"E32")])],"isStart":false});Q1=makeQuery(id+"F26.imprint","IMPRINT",FACE,{"disambiguationData":[TD([[makeQuery(id+"F26.imprint","IMPRINT",EDGE,{"derivedFrom":subQ3}),1.0]])]});}
            extrude(context, id + "F27", {"entities" : qUnion([Q0, Q1]), "depth" : 127 * mm, "offsetDistance" : 25.4 * mm});
        }
        {
            var Q0;
            Q0=makeQuery(id+"F27.opExtrude","CAP_FACE",FACE,{"disambiguationData":[OSD([sQuery(id+"F26.wireOp",EDGE,"E49"),sQuery(id+"F26.wireOp",EDGE,"E50"),sQuery(id+"F26.wireOp",EDGE,"E51"),sQuery(id+"F26.wireOp",EDGE,"E52")])],"isStart":false});
            var sketch = newSketch(context, id + "F28", { "sketchPlane" : qUnion([Q0])});
            skLineSegment(sketch, "E53", {"start": v(-6546.85, 1479.55) * mm, "end": v(-6546.85, 1502.74) * mm});
            skLineSegment(sketch, "E54", {"start": v(-6546.85, 1502.74) * mm, "end": v(-5595.94, 842.39) * mm});
            skLineSegment(sketch, "E55.0", {"start": v(-5632.45, 844.55) * mm, "end": v(-6546.85, 1479.55) * mm});
            skLineSegment(sketch, "E56", {"start": v(-5632.45, 844.55) * mm, "end": v(-5595.94, 819.2) * mm});
            skLineSegment(sketch, "E57", {"start": v(-5595.94, 819.2) * mm, "end": v(-5595.94, 842.39) * mm});
            skSolve(sketch);
        }
        {
            var Q0;
            Q0 = qSketchRegion(id + "F28", true);
            extrude(context, id + "F29", {"entities" : qUnion([Q0]), "operationType" : NewBodyOperationType.ADD, "depth" : 25.4 * mm, "offsetDistance" : 25.4 * mm, "hasSecondDirection" : true, "secondDirectionOppositeDirection" : true, "secondDirectionDepth" : 158.75 * mm});
        }
        {
            var Q0;
            {var subQ0=sQuery(id+"F4.wireOp",EDGE,"E15.1");var subQ1=sQuery(id+"F0.wireOp",EDGE,"E4");var subQ3=sQuery(id+"F4.wireOp",EDGE,"E15.0");var subQ4=sQuery(id+"F4.wireOp",EDGE,"E18.0");var subQ5=sQuery(id+"F4.wireOp",EDGE,"E14.0");var subQ6=sQuery(id+"F0.wireOp",EDGE,"E0.bottom");var subQ8=sQuery(id+"F4.wireOp",EDGE,"E13.0");var subQ9=sQuery(id+"F4.wireOp",EDGE,"E16.0");var subQ10=sQuery(id+"F4.wireOp",EDGE,"E11.0");var subQ11=sQuery(id+"F4.wireOp",EDGE,"E12.0");var subQ12=sQuery(id+"F2.wireOp",EDGE,"E7.0");var subQ14=sQuery(id+"F2.wireOp",EDGE,"E5.0");var subQ16=sQuery(id+"F4.wireOp",EDGE,"E15.2");var subQ17=sQuery(id+"F4.wireOp",EDGE,"E15.3");var subQ18=sQuery(id+"F4.wireOp",EDGE,"E17");var subQ19=sQuery(id+"F4.wireOp",EDGE,"E19");var subQ21=sQuery(id+"F2.wireOp",EDGE,"E10");var subQ22=sQuery(id+"F2.wireOp",EDGE,"E9");var subQ23=sQuery(id+"F2.wireOp",EDGE,"E8.0");var subQ24=sQuery(id+"F2.wireOp",EDGE,"E7.1");var subQ25=sQuery(id+"F2.wireOp",EDGE,"E6.0");var subQ26=sQuery(id+"F0.wireOp",EDGE,"E0.left");var subQ27=makeQuery(id+"F3.opExtrude","CAP_FACE",FACE,{"disambiguationData":[OSD([subQ6,subQ26,subQ1,subQ14,subQ25,subQ12,subQ24,subQ23,subQ22,subQ21])],"isStart":false});Q0=makeQuery(id+"F10.boolean.opBoolean","SPLIT",FACE,{"disambiguationData":[TD([makeQuery(id+"F5.opExtrude","SWEPT_FACE",FACE,{"disambiguationData":[OSD([subQ11])]})])],"derivedFrom":makeQuery(id+"F8.opBoolean","MERGE",FACE,{"derivedFrom":[makeQuery(id+"F5.opExtrude","CAP_FACE",FACE,{"disambiguationData":[OSD([subQ10,subQ11,subQ8,subQ5,subQ3,subQ0,subQ16,subQ17,subQ9,subQ18,subQ4,subQ19])],"isStart":false}),makeQuery(id+"F7.boolean.opBoolean","SPLIT",FACE,{"disambiguationData":[TD([makeQuery(id+"F3.opExtrude","SWEPT_FACE",FACE,{"disambiguationData":[OSD([subQ25])]})])],"derivedFrom":subQ27}),makeQuery(id+"F7.boolean.opBoolean","SPLIT",FACE,{"disambiguationData":[TD([makeQuery(id+"F3.opExtrude","SWEPT_FACE",FACE,{"disambiguationData":[OSD([subQ21])]})])],"derivedFrom":subQ27})]})});}
            var sketch = newSketch(context, id + "F30", { "sketchPlane" : qUnion([Q0])});
            skLineSegment(sketch, "E58", {"start": v(-6718.3, 8870.95) * mm, "end": v(-5537.2, 8870.95) * mm});
            skLineSegment(sketch, "E59", {"start": v(-5537.2, 8870.95) * mm, "end": v(-5537.2, 6254.75) * mm});
            skLineSegment(sketch, "E60", {"start": v(-5537.2, 6254.75) * mm, "end": v(-6546.85, 6254.75) * mm});
            skLineSegment(sketch, "E61", {"start": v(-6546.85, 6254.75) * mm, "end": v(-6546.85, -57.15) * mm});
            skLineSegment(sketch, "E62.0", {"start": v(-6699.25, -57.15) * mm, "end": v(-5746.75, -57.15) * mm});
            skLineSegment(sketch, "E63.0", {"start": v(-6699.25, -57.15) * mm, "end": v(-6699.25, 6388.1) * mm});
            skLineSegment(sketch, "E64.0", {"start": v(-5670.55, 6388.1) * mm, "end": v(-6699.25, 6388.1) * mm});
            skLineSegment(sketch, "E65.0", {"start": v(-5670.55, 8737.6) * mm, "end": v(-5670.55, 6388.1) * mm});
            skLineSegment(sketch, "E66.0", {"start": v(-6718.3, 8737.6) * mm, "end": v(-5670.55, 8737.6) * mm});
            skLineSegment(sketch, "E67.0", {"start": v(-6718.3, 8870.95) * mm, "end": v(-6718.3, 8737.6) * mm});
            skSolve(sketch);
        }
        {
            var Q0;
            Q0 = qSketchRegion(id + "F30", true);
            extrude(context, id + "F31", {"entities" : qUnion([Q0]), "depth" : 3200.4 * mm, "offsetDistance" : 25.4 * mm});
        }
        {
            var Q0;
            {var subQ0=sQuery(id+"F4.wireOp",EDGE,"E19");var subQ1=sQuery(id+"F0.wireOp",EDGE,"E0.left");var subQ3=sQuery(id+"F0.wireOp",EDGE,"E0.bottom");var subQ5=sQuery(id+"F2.wireOp",EDGE,"E8.0");var subQ7=sQuery(id+"F4.wireOp",EDGE,"E17");var subQ8=sQuery(id+"F0.wireOp",EDGE,"E4");var subQ10=sQuery(id+"F2.wireOp",EDGE,"E5.0");var subQ12=sQuery(id+"F2.wireOp",EDGE,"E7.1");var subQ14=sQuery(id+"F2.wireOp",EDGE,"E6.0");var subQ15=makeQuery(id+"F3.opExtrude","SWEPT_FACE",FACE,{"disambiguationData":[OSD([subQ14])]});var subQ16=sQuery(id+"F2.wireOp",EDGE,"E7.0");var subQ19=sQuery(id+"F2.wireOp",EDGE,"E10");var subQ20=sQuery(id+"F2.wireOp",EDGE,"E9");var subQ21=makeQuery(id+"F3.opExtrude","CAP_FACE",FACE,{"disambiguationData":[OSD([subQ3,subQ1,subQ8,subQ10,subQ14,subQ16,subQ12,subQ5,subQ20,subQ19])],"isStart":false});Q0=makeQuery(id+"F10.boolean.opBoolean","SPLIT",FACE,{"disambiguationData":[TD([subQ15])],"derivedFrom":makeQuery(id+"F8.opBoolean","MERGE",FACE,{"derivedFrom":[makeQuery(id+"F5.opExtrude","CAP_FACE",FACE,{"disambiguationData":[OSD([sQuery(id+"F4.wireOp",EDGE,"E11.0"),sQuery(id+"F4.wireOp",EDGE,"E12.0"),sQuery(id+"F4.wireOp",EDGE,"E13.0"),sQuery(id+"F4.wireOp",EDGE,"E14.0"),sQuery(id+"F4.wireOp",EDGE,"E15.0"),sQuery(id+"F4.wireOp",EDGE,"E15.1"),sQuery(id+"F4.wireOp",EDGE,"E15.2"),sQuery(id+"F4.wireOp",EDGE,"E15.3"),sQuery(id+"F4.wireOp",EDGE,"E16.0"),subQ7,sQuery(id+"F4.wireOp",EDGE,"E18.0"),subQ0])],"isStart":false}),makeQuery(id+"F7.boolean.opBoolean","SPLIT",FACE,{"disambiguationData":[TD([subQ15])],"derivedFrom":subQ21}),makeQuery(id+"F7.boolean.opBoolean","SPLIT",FACE,{"disambiguationData":[TD([makeQuery(id+"F3.opExtrude","SWEPT_FACE",FACE,{"disambiguationData":[OSD([subQ19])]})])],"derivedFrom":subQ21})]})});}
            var sketch = newSketch(context, id + "F32", { "sketchPlane" : qUnion([Q0])});
            skLineSegment(sketch, "E68.0", {"start": v(-6807.2, 8737.6) * mm, "end": v(-6807.2, 11233.15) * mm});
            skLineSegment(sketch, "E69.0", {"start": v(190.5, -146.05) * mm, "end": v(190.5, 11233.15) * mm});
            skLineSegment(sketch, "E70", {"start": v(190.5, 11233.15) * mm, "end": v(-6807.2, 11233.15) * mm});
            skPoint(sketch, "E71.0", {"position": v(-660.4, -146.05) * mm});
            skLineSegment(sketch, "E72", {"start": v(190.5, -146.05) * mm, "end": v(-660.4, -146.05) * mm});
            skLineSegment(sketch, "E73.0", {"start": v(209.55, -165.1) * mm, "end": v(-6699.25, -165.1) * mm});
            skLineSegment(sketch, "E73.1", {"start": v(209.55, -165.1) * mm, "end": v(209.55, 11252.2) * mm});
            skLineSegment(sketch, "E73.2", {"start": v(209.55, 11252.2) * mm, "end": v(-6826.25, 11252.2) * mm});
            skLineSegment(sketch, "E73.3", {"start": v(-6826.25, 8737.6) * mm, "end": v(-6826.25, 11252.2) * mm});
            skLineSegment(sketch, "E74", {"start": v(-6807.2, 8737.6) * mm, "end": v(-6826.25, 8737.6) * mm});
            skLineSegment(sketch, "E75", {"start": v(-660.4, -146.05) * mm, "end": v(-6699.25, -146.05) * mm});
            skPoint(sketch, "E76.0", {"position": v(-6699.25, -146.05) * mm});
            skLineSegment(sketch, "E77", {"start": v(-6699.25, -146.05) * mm, "end": v(-6699.25, -165.1) * mm});
            skSolve(sketch);
        }
        {
            var Q0;
            Q0 = qSketchRegion(id + "F32", true);
            extrude(context, id + "F33", {"entities" : qUnion([Q0]), "depth" : 3200.4 * mm, "offsetDistance" : 25.4 * mm});
        }
        {
            var Q0;
            Q0=makeQuery(id+"F33.opExtrude","SWEPT_FACE",FACE,{"disambiguationData":[OSD([sQuery(id+"F32.wireOp",EDGE,"E73.0")])]});
            var sketch = newSketch(context, id + "F34", { "sketchPlane" : qUnion([Q0])});
            skPoint(sketch, "E78.0", {"position": v(-5746.75, 152.4) * mm});
            skPoint(sketch, "E79.0", {"position": v(-660.4, 152.4) * mm});
            skLineSegment(sketch, "E80.bottom", {"start": v(-5746.75, 152.4) * mm, "end": v(-660.4, 152.4) * mm});
            skLineSegment(sketch, "E80.top", {"start": v(-5746.75, 2438.4) * mm, "end": v(-660.4, 2438.4) * mm});
            skLineSegment(sketch, "E80.left", {"start": v(-5746.75, 152.4) * mm, "end": v(-5746.75, 2438.4) * mm});
            skLineSegment(sketch, "E80.right", {"start": v(-660.4, 152.4) * mm, "end": v(-660.4, 2438.4) * mm});
            skSolve(sketch);
        }
        {
            var Q0;
            Q0 = qSketchRegion(id + "F34", true);
            extrude(context, id + "F35", {"entities" : qUnion([Q0]), "operationType" : NewBodyOperationType.REMOVE, "endBound" : BoundingType.UP_TO_NEXT, "oppositeDirection" : true, "depth" : 25.4 * mm, "offsetDistance" : 25.4 * mm});
        }
        {
            var Q0;
            Q0=makeQuery(id+"F33.opExtrude","SWEPT_FACE",FACE,{"disambiguationData":[OSD([sQuery(id+"F32.wireOp",EDGE,"E73.3")])]});
            var sketch = newSketch(context, id + "F36", { "sketchPlane" : qUnion([Q0])});
            skPoint(sketch, "E81.0", {"position": v(-10490.2, 152.4) * mm});
            skPoint(sketch, "E82.0", {"position": v(-9499.6, 152.4) * mm});
            skLineSegment(sketch, "E83.bottom", {"start": v(-10490.2, 152.4) * mm, "end": v(-9499.6, 152.4) * mm});
            skLineSegment(sketch, "E83.top", {"start": v(-10490.2, 2438.4) * mm, "end": v(-9499.6, 2438.4) * mm});
            skLineSegment(sketch, "E83.left", {"start": v(-10490.2, 152.4) * mm, "end": v(-10490.2, 2438.4) * mm});
            skLineSegment(sketch, "E83.right", {"start": v(-9499.6, 152.4) * mm, "end": v(-9499.6, 2438.4) * mm});
            skSolve(sketch);
        }
        {
            var Q0;
            Q0 = qSketchRegion(id + "F36", true);
            extrude(context, id + "F37", {"entities" : qUnion([Q0]), "operationType" : NewBodyOperationType.REMOVE, "endBound" : BoundingType.UP_TO_NEXT, "oppositeDirection" : true, "depth" : 25.4 * mm, "offsetDistance" : 25.4 * mm});
        }
        {
            var Q0;
            Q0=makeQuery(id+"F31.opExtrude","SWEPT_FACE",FACE,{"disambiguationData":[OSD([sQuery(id+"F30.wireOp",EDGE,"E61")])]});
            var sketch = newSketch(context, id + "F38", { "sketchPlane" : qUnion([Q0])});
            skPoint(sketch, "E84.0", {"position": v(6254.75, 755.65) * mm});
            skPoint(sketch, "E85.0", {"position": v(5251.45, 755.65) * mm});
            skLineSegment(sketch, "E86.bottom", {"start": v(6254.75, 755.65) * mm, "end": v(5251.45, 755.65) * mm});
            skLineSegment(sketch, "E86.top", {"start": v(6254.75, 2889.25) * mm, "end": v(5251.45, 2889.25) * mm});
            skLineSegment(sketch, "E86.left", {"start": v(6254.75, 755.65) * mm, "end": v(6254.75, 2889.25) * mm});
            skLineSegment(sketch, "E86.right", {"start": v(5251.45, 755.65) * mm, "end": v(5251.45, 2889.25) * mm});
            skSolve(sketch);
        }
        {
            var Q0;
            Q0 = qSketchRegion(id + "F38", true);
            extrude(context, id + "F39", {"entities" : qUnion([Q0]), "operationType" : NewBodyOperationType.REMOVE, "endBound" : BoundingType.UP_TO_NEXT, "oppositeDirection" : true, "depth" : 25.4 * mm, "offsetDistance" : 25.4 * mm});
        }
        {
            var Q0;
            Q0=makeQuery(id+"F31.opExtrude","CAP_FACE",FACE,{"disambiguationData":[OSD([sQuery(id+"F30.wireOp",EDGE,"E58"),sQuery(id+"F30.wireOp",EDGE,"E59"),sQuery(id+"F30.wireOp",EDGE,"E60"),sQuery(id+"F30.wireOp",EDGE,"E61"),sQuery(id+"F30.wireOp",EDGE,"E62.0"),sQuery(id+"F30.wireOp",EDGE,"E63.0"),sQuery(id+"F30.wireOp",EDGE,"E64.0"),sQuery(id+"F30.wireOp",EDGE,"E65.0"),sQuery(id+"F30.wireOp",EDGE,"E66.0"),sQuery(id+"F30.wireOp",EDGE,"E67.0")])],"isStart":false});
            var sketch = newSketch(context, id + "F40", { "sketchPlane" : qUnion([Q0])});
            skLineSegment(sketch, "E87.0", {"start": v(-6546.85, 6254.75) * mm, "end": v(-6546.85, 0) * mm});
            skLineSegment(sketch, "E88.0", {"start": v(-5537.2, 6254.75) * mm, "end": v(-6546.85, 6254.75) * mm});
            skLineSegment(sketch, "E89.0", {"start": v(-5537.2, 8870.95) * mm, "end": v(-5537.2, 6254.75) * mm});
            skLineSegment(sketch, "E90.0", {"start": v(-6597.65, 8870.95) * mm, "end": v(-5537.2, 8870.95) * mm});
            skLineSegment(sketch, "E91.0", {"start": v(-6597.65, 8870.95) * mm, "end": v(-6597.65, 10490.2) * mm});
            skLineSegment(sketch, "E92.0", {"start": v(-6597.65, 10490.2) * mm, "end": v(-6597.65, 11023.6) * mm});
            skLineSegment(sketch, "E93.0", {"start": v(0, 11023.6) * mm, "end": v(-6597.65, 11023.6) * mm});
            skLineSegment(sketch, "E94.0", {"start": v(0, 0) * mm, "end": v(0, 11023.6) * mm});
            skLineSegment(sketch, "E95.0", {"start": v(0, 0) * mm, "end": v(-5746.75, 0) * mm});
            skLineSegment(sketch, "E96.0", {"start": v(-5746.75, 0) * mm, "end": v(-6546.85, 0) * mm});
            skPoint(sketch, "E97.orphan", {"position": v(-6597.65, 0) * mm});
            skPoint(sketch, "E98.orphan", {"position": v(-6546.85, -57.15) * mm});
            skPoint(sketch, "E99.orphan", {"position": v(-6718.3, 8870.95) * mm});
            skPoint(sketch, "E100.orphan", {"position": v(-6597.65, 8839.2) * mm});
            skPoint(sketch, "E101.orphan", {"position": v(-6597.65, 9499.6) * mm});
            skPoint(sketch, "E102.orphan", {"position": v(-660.4, 0) * mm});
            skSolve(sketch);
        }
        {
            var Q0;
            Q0 = qSketchRegion(id + "F40", true);
            extrude(context, id + "F41", {"entities" : qUnion([Q0]), "depth" : 15.88 * mm, "offsetDistance" : 25.4 * mm});
        }
    });
